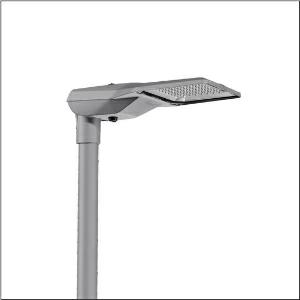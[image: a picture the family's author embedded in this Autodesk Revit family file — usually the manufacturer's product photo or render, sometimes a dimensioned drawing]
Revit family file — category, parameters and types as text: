
# Revit family: streetlight_sl_21_midi___stw1_0a_5xe3e63t08nb_c3f7
name_source: partatom
category: Lighting Fixtures
units: mm (PartAtom-declared; Revit-internal decimal feet)

## family parameters
Cut with Voids When Loaded = No
Host = Face
Light Source = No
Part Type = Normal
Room Calculation Point = No
Round Connector Dimension = Use Diameter
Shared = No

## types (1)
- --- (1 x LED, 20350 lm, 151.2 W, 2700K)
    Apparent Load = 151 VA
    CIE Flux Codes = 39 75 98 100 100
    Color Rendering = 70
    Color Temperature = 2700K
    Default Elevation = 1800 mm
    Description = Streetlight SL 21 midi, mast luminaire, primary light control with lens, of PMMA, primary optical cover: cover, of toughened safety glass, transparent, light distribution: STW1.0a, light emission: direct distribution, primary light characteristic: asymmetric, installation type: side-entry, post-top, LED, High Power LED, rated luminous flux: 20.350lm, luminous efficacy: 135lm/W, light colour: 727, colour temperature: 2700K, control gear: D4i, control: overheat protection, constant luminous flux control, time-dependent luminous flux control, flexible luminous flux parameterisation, pre-setting: logarithmic dimming characteristic, mains connection: 230..240V, AC, 50/60Hz, start of lifetime: 151W, end of service life: 157W, reduction: 70W, luminaire housing, of diecast aluminium, powder-coated, SITECO metallic grey (DB 702S), corrosivity category C5 high according to DIN EN ISO 12944, please order mast flange separately, inclination adjustable: 0°, 5°, 10°, 15°, sealing non-destructively replaceable, multi-level sealing system, length: 644mm, width: 335mm, height: 110mm, mast flange for spigot size: 42mm (side-entry): 5XC10008XM4, 60/48mm (side-entry/post-top): 5XC10108XM2, 76/60mm (side-entry/post-top): 5XC10108XM1, mounting height: 4..8m, Smart Interface below and above, protection rating (complete): IP66, insulation class (complete): insulation class II (safety insulation), certification: CE, ENEC, ENEC+, VDE, impact resistance: IK10, permissible operating ambient temperature for outdoor applications: -40..+50°C, standard-compliant lighting for roads and squares, packaging unit: 1 piece

Light Distribution: STW1.0a
    Height = 111 mm
    Lamp = 1 x LED
    Lamp Light Flux = 20350 lm
    Lamp Power = 151.2 W
    Lamp count = 1
    Length = 644 mm
    Luminous efficacy = 135 lm/W
    Manufacturer = Siteco
    ModVariant = No
    Model = 5XE3E63T08NB
    Mounting Place = Pole
    Mounting Type = Pole top
    Number of Poles = 1
    OnlyDefault = Yes
    Power Factor = 1
    Product Name = Streetlight SL 21 midi | STW1.0a
    Product group = mast luminaire | pylon top
    ProductGroupID = 6100
    Protection Class = Protection class II
    Protection Degree = IP 66
    RLX_Detail_Level = 1
    RLX_Emergency_Light_Flux = 0 lm
    RLX_Emergency_Type = 0
    RLX_Emergency_Type_DB = No
    RlxData = <blob elided: 27209 chars, md5=a518db4d>
    Socket = socket
    Standby Power = 0 W
    System Light Flux = 20350 lm
    System Power = 151 W
    Type Comments = factory setting: luminous flux: 100 % | dim-lin: 254 | 802 mA
    Type Image = l_1004304.jpg
    URL = http://relux.com
    VarID = @adj_170529
    Voltage = 0 V
    Weight = 0.00 kg
    Width = 336 mm

## geometry (parser evidence)
native form markers: Blend x4, Sweep x11
no freeform markers — native parametric forms only
